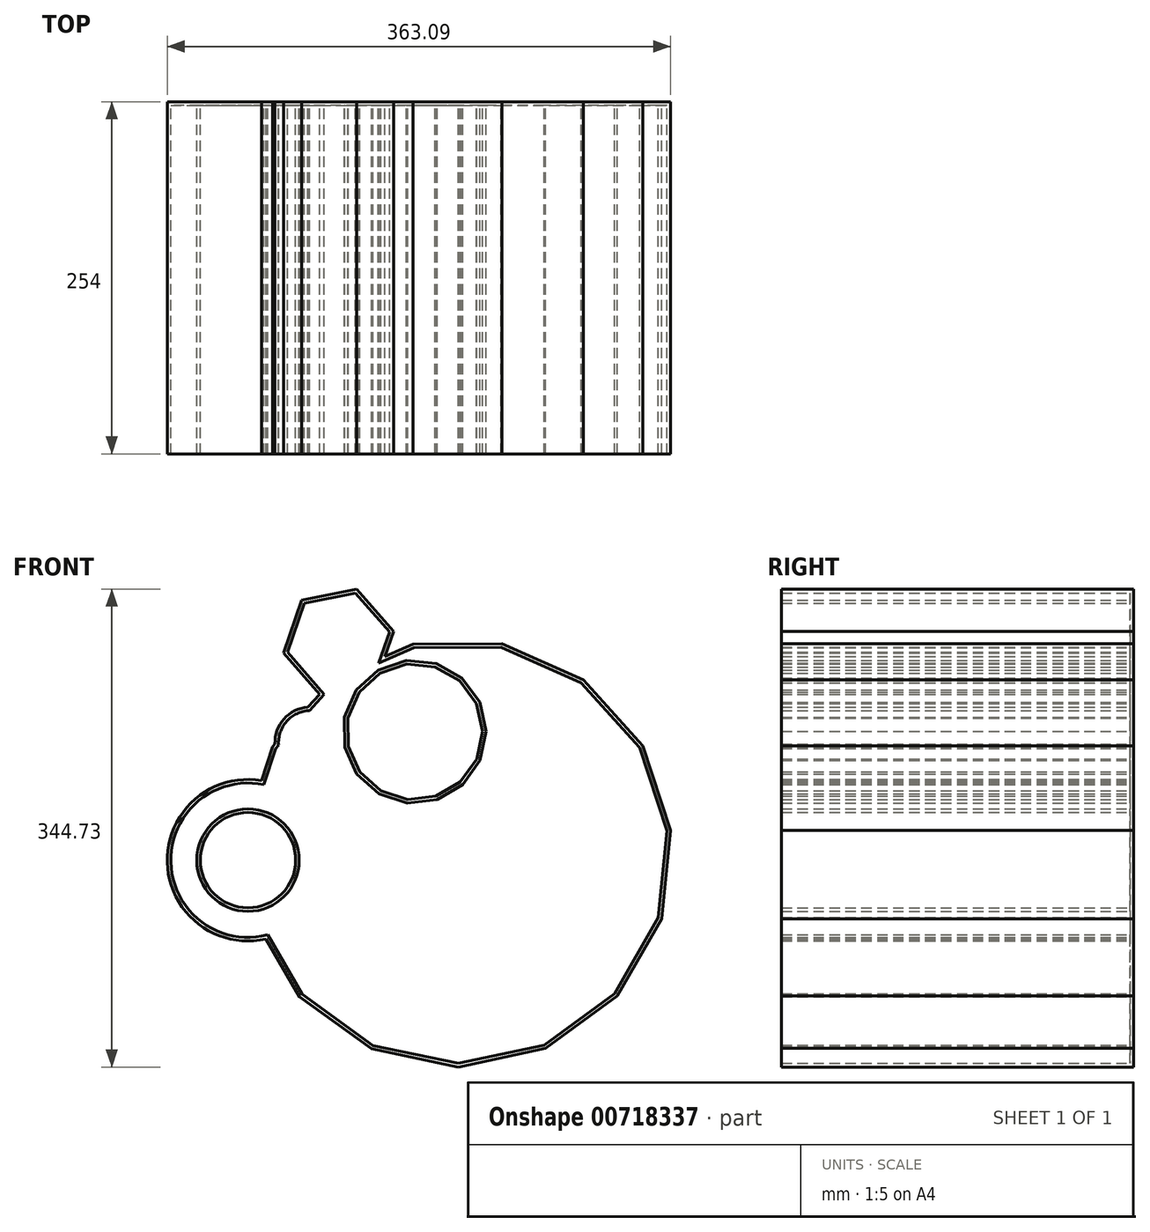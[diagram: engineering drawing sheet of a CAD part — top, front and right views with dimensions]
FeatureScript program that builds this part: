
annotation { "Feature Type Name" : "Feature", "Feature Type Description" : "" }
export const myFeature = defineFeature(function(context is Context, id is Id, definition is map)
    precondition{}
    {
        {
            var Q0;
            Q0=qCreatedBy(makeId("Front.planeOp"),FACE);
            var sketch = newSketch(context, id + "F0", { "sketchPlane" : qUnion([Q0])});
            skCircle(sketch, "E0", {"center": v(-245.75, -122.9) * mm, "radius": 34.4 * mm});
            skCircle(sketch, "E1", {"center": v(-245.75, -122.9) * mm, "radius": 58.22 * mm});
            skArc(sketch, "E2", {"start": v(-182.55, -19.53) * mm, "mid": v(-226.23, -40.3) * mm, "end": v(-179.93, -54.3) * mm});
            skArc(sketch, "E3", {"start": v(-182.55, -19.53) * mm, "mid": v(-177.78, -20.54) * mm, "end": v(-174.71, -16.75) * mm});
            skArc(sketch, "E4", {"start": v(-108.9, -64.08) * mm, "mid": v(-156.13, -71.74) * mm, "end": v(-152.25, -119.42) * mm});
            skCircle(sketch, "E5.cCircle", {"center": v(-180.46, 34.35) * mm, "radius": 35.01 * mm, "construction": true});
            skLineSegment(sketch, "E5.0", {"start": v(-153.84, 3.92) * mm, "end": v(-193.5, -3.92) * mm});
            skLineSegment(sketch, "E5.1", {"start": v(-193.5, -3.92) * mm, "end": v(-220.12, 26.5) * mm});
            skLineSegment(sketch, "E5.2", {"start": v(-220.12, 26.5) * mm, "end": v(-207.08, 64.78) * mm});
            skLineSegment(sketch, "E5.3", {"start": v(-207.08, 64.78) * mm, "end": v(-167.42, 72.62) * mm});
            skLineSegment(sketch, "E5.4", {"start": v(-167.42, 72.62) * mm, "end": v(-140.8, 42.19) * mm});
            skLineSegment(sketch, "E5.5", {"start": v(-140.8, 42.19) * mm, "end": v(-153.84, 3.92) * mm});
            skPoint(sketch, "E5.0.midPoint", {"position": v(-173.67, 0) * mm});
            skCircle(sketch, "E6.cCircle", {"center": v(-125.61, -30.26) * mm, "radius": 47.95 * mm, "construction": true});
            skLineSegment(sketch, "E6.0", {"start": v(-149.86, -72.86) * mm, "end": v(-165.1, -59.32) * mm});
            skLineSegment(sketch, "E6.1", {"start": v(-165.1, -59.32) * mm, "end": v(-173.5, -40.75) * mm});
            skLineSegment(sketch, "E6.2", {"start": v(-173.5, -40.75) * mm, "end": v(-173.63, -20.36) * mm});
            skLineSegment(sketch, "E6.3", {"start": v(-173.63, -20.36) * mm, "end": v(-165.45, -1.7) * mm});
            skLineSegment(sketch, "E6.4", {"start": v(-165.45, -1.7) * mm, "end": v(-150.4, 12.04) * mm});
            skLineSegment(sketch, "E6.5", {"start": v(-150.4, 12.04) * mm, "end": v(-131.04, 18.46) * mm});
            skLineSegment(sketch, "E6.6", {"start": v(-131.04, 18.46) * mm, "end": v(-110.76, 16.46) * mm});
            skLineSegment(sketch, "E6.7", {"start": v(-110.76, 16.46) * mm, "end": v(-93.04, 6.38) * mm});
            skLineSegment(sketch, "E6.8", {"start": v(-93.04, 6.38) * mm, "end": v(-80.96, -10.04) * mm});
            skLineSegment(sketch, "E6.9", {"start": v(-80.96, -10.04) * mm, "end": v(-76.6, -29.95) * mm});
            skLineSegment(sketch, "E6.10", {"start": v(-76.6, -29.95) * mm, "end": v(-80.7, -49.91) * mm});
            skLineSegment(sketch, "E6.11", {"start": v(-80.7, -49.91) * mm, "end": v(-92.58, -66.48) * mm});
            skLineSegment(sketch, "E6.12", {"start": v(-92.58, -66.48) * mm, "end": v(-110.17, -76.78) * mm});
            skLineSegment(sketch, "E6.13", {"start": v(-110.17, -76.78) * mm, "end": v(-130.43, -79.04) * mm});
            skLineSegment(sketch, "E6.14", {"start": v(-130.43, -79.04) * mm, "end": v(-149.86, -72.86) * mm});
            skPoint(sketch, "E6.0.midPoint", {"position": v(-157.48, -66.1) * mm});
            skCircle(sketch, "E7.cCircle", {"center": v(-94.28, -117.84) * mm, "radius": 150.9 * mm, "construction": true});
            skLineSegment(sketch, "E7.0", {"start": v(-247.75, -102.08) * mm, "end": v(-228.07, -41.02) * mm});
            skLineSegment(sketch, "E7.1", {"start": v(-228.07, -41.02) * mm, "end": v(-185.26, 6.76) * mm});
            skLineSegment(sketch, "E7.2", {"start": v(-185.26, 6.76) * mm, "end": v(-126.72, 33) * mm});
            skLineSegment(sketch, "E7.3", {"start": v(-126.72, 33) * mm, "end": v(-62.57, 33.15) * mm});
            skLineSegment(sketch, "E7.4", {"start": v(-62.57, 33.15) * mm, "end": v(-3.9, 7.2) * mm});
            skLineSegment(sketch, "E7.5", {"start": v(-3.9, 7.2) * mm, "end": v(39.14, -40.37) * mm});
            skLineSegment(sketch, "E7.6", {"start": v(39.14, -40.37) * mm, "end": v(59.12, -101.34) * mm});
            skLineSegment(sketch, "E7.7", {"start": v(59.12, -101.34) * mm, "end": v(52.57, -165.15) * mm});
            skLineSegment(sketch, "E7.8", {"start": v(52.57, -165.15) * mm, "end": v(20.63, -220.79) * mm});
            skLineSegment(sketch, "E7.9", {"start": v(20.63, -220.79) * mm, "end": v(-31.18, -258.62) * mm});
            skLineSegment(sketch, "E7.10", {"start": v(-31.18, -258.62) * mm, "end": v(-93.9, -272.11) * mm});
            skLineSegment(sketch, "E7.11", {"start": v(-93.9, -272.11) * mm, "end": v(-156.68, -258.93) * mm});
            skLineSegment(sketch, "E7.12", {"start": v(-156.68, -258.93) * mm, "end": v(-208.68, -221.35) * mm});
            skLineSegment(sketch, "E7.13", {"start": v(-208.68, -221.35) * mm, "end": v(-240.89, -165.87) * mm});
            skLineSegment(sketch, "E7.14", {"start": v(-240.89, -165.87) * mm, "end": v(-247.75, -102.08) * mm});
            skPoint(sketch, "E7.0.midPoint", {"position": v(-237.91, -71.55) * mm});
            skSolve(sketch);
        }
        {
            var Q0;
            Q0 = qSketchRegion(id + "F0", true);
            extrude(context, id + "F1", {"entities" : qUnion([Q0]), "depth" : 254 * mm, "offsetDistance" : 25.4 * mm});
        }
        {
            var Q0;
            Q0=makeQuery(id+"F1.opExtrude","CAP_FACE",FACE,{"disambiguationData":[OSD([sQuery(id+"F0.wireOp",EDGE,"E0"),sQuery(id+"F0.wireOp",EDGE,"E1"),sQuery(id+"F0.wireOp",EDGE,"E2"),sQuery(id+"F0.wireOp",EDGE,"E5.1"),sQuery(id+"F0.wireOp",EDGE,"E5.2"),sQuery(id+"F0.wireOp",EDGE,"E5.3"),sQuery(id+"F0.wireOp",EDGE,"E5.4"),sQuery(id+"F0.wireOp",EDGE,"E5.5"),sQuery(id+"F0.wireOp",EDGE,"E6.0"),sQuery(id+"F0.wireOp",EDGE,"E6.1"),sQuery(id+"F0.wireOp",EDGE,"E6.2"),sQuery(id+"F0.wireOp",EDGE,"E6.3"),sQuery(id+"F0.wireOp",EDGE,"E6.4"),sQuery(id+"F0.wireOp",EDGE,"E6.5"),sQuery(id+"F0.wireOp",EDGE,"E6.6"),sQuery(id+"F0.wireOp",EDGE,"E6.7"),sQuery(id+"F0.wireOp",EDGE,"E6.8"),sQuery(id+"F0.wireOp",EDGE,"E6.9"),sQuery(id+"F0.wireOp",EDGE,"E6.10"),sQuery(id+"F0.wireOp",EDGE,"E6.11"),sQuery(id+"F0.wireOp",EDGE,"E6.12"),sQuery(id+"F0.wireOp",EDGE,"E6.13"),sQuery(id+"F0.wireOp",EDGE,"E6.14"),sQuery(id+"F0.wireOp",EDGE,"E7.0"),sQuery(id+"F0.wireOp",EDGE,"E7.1"),sQuery(id+"F0.wireOp",EDGE,"E7.2"),sQuery(id+"F0.wireOp",EDGE,"E7.3"),sQuery(id+"F0.wireOp",EDGE,"E7.4"),sQuery(id+"F0.wireOp",EDGE,"E7.5"),sQuery(id+"F0.wireOp",EDGE,"E7.6"),sQuery(id+"F0.wireOp",EDGE,"E7.7"),sQuery(id+"F0.wireOp",EDGE,"E7.8"),sQuery(id+"F0.wireOp",EDGE,"E7.9"),sQuery(id+"F0.wireOp",EDGE,"E7.10"),sQuery(id+"F0.wireOp",EDGE,"E7.11"),sQuery(id+"F0.wireOp",EDGE,"E7.12"),sQuery(id+"F0.wireOp",EDGE,"E7.13")])],"isStart":false});
            shell(context, id + "F2", {"entities" : qUnion([Q0]), "thickness" : 2.54 * mm});
        }
    });
